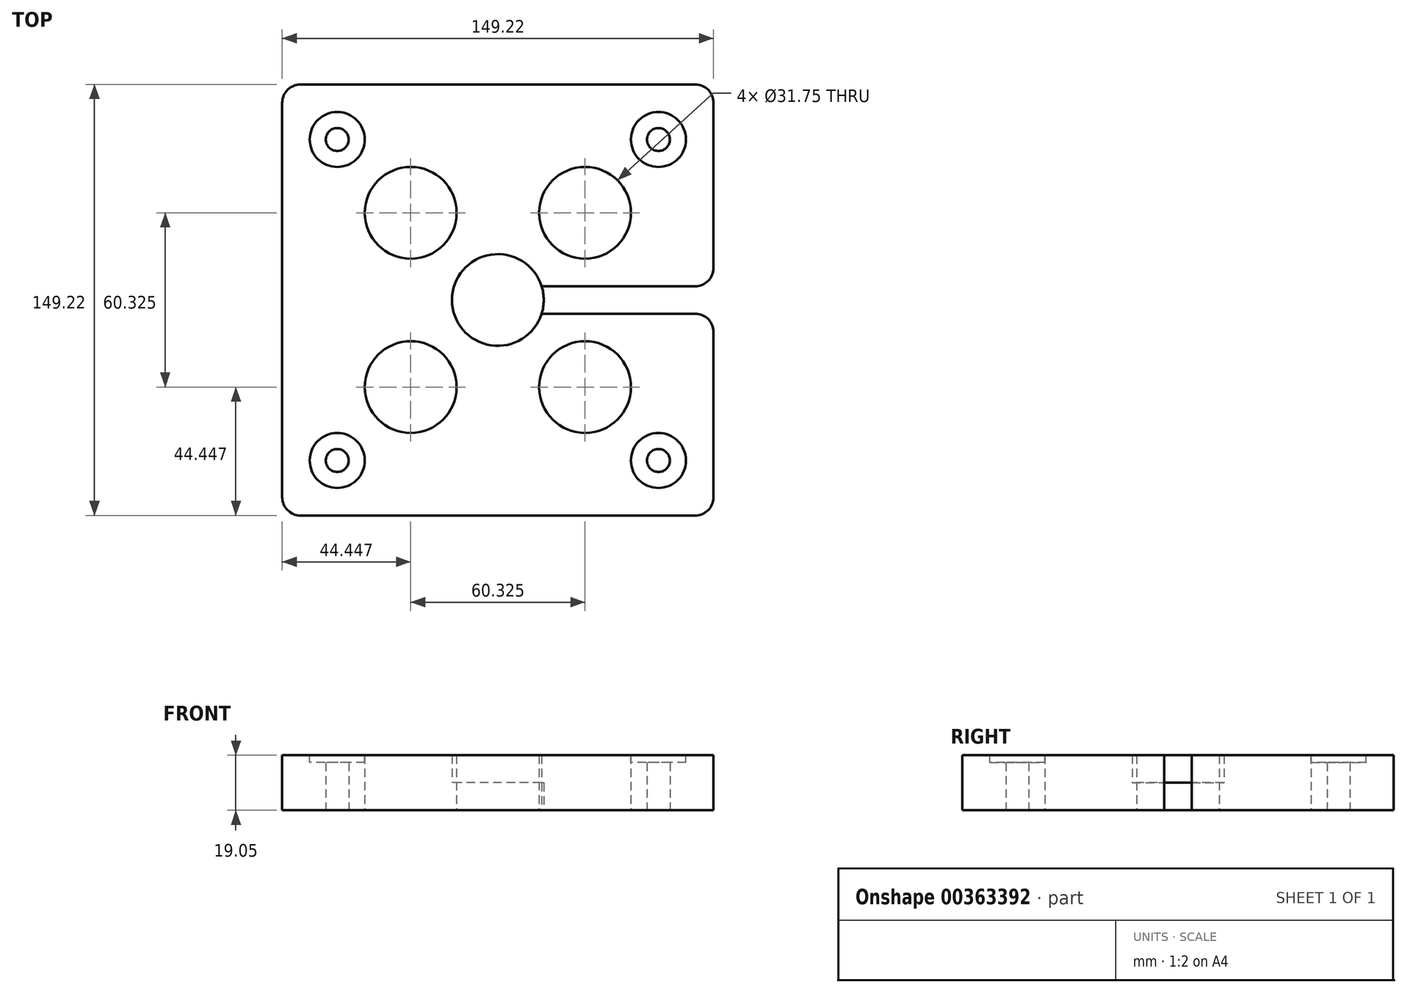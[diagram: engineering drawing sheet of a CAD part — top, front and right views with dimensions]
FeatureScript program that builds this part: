
annotation { "Feature Type Name" : "Feature", "Feature Type Description" : "" }
export const myFeature = defineFeature(function(context is Context, id is Id, definition is map)
    precondition{}
    {
        {
            var Q0;
            Q0=qCreatedBy(makeId("Top.planeOp"),FACE);
            var sketch = newSketch(context, id + "F0", { "sketchPlane" : qUnion([Q0])});
            skLineSegment(sketch, "E0.bottom", {"start": v(68.26, -74.61) * mm, "end": v(-68.26, -74.61) * mm});
            skLineSegment(sketch, "E0.top", {"start": v(68.26, 74.61) * mm, "end": v(-68.26, 74.61) * mm});
            skLineSegment(sketch, "E0.left", {"start": v(74.61, -68.26) * mm, "end": v(74.61, 68.26) * mm});
            skLineSegment(sketch, "E0.right", {"start": v(-74.61, -68.26) * mm, "end": v(-74.61, 68.26) * mm});
            skPoint(sketch, "E0.middle", {"position": v(0, 0) * mm});
            skCircle(sketch, "E1", {"center": v(0, 0) * mm, "radius": 15.88 * mm});
            skCircle(sketch, "E2", {"center": v(-30.16, 30.16) * mm, "radius": 15.88 * mm});
            skCircle(sketch, "E3", {"center": v(30.16, 30.16) * mm, "radius": 15.88 * mm});
            skCircle(sketch, "E4", {"center": v(-30.16, -30.16) * mm, "radius": 15.88 * mm});
            skCircle(sketch, "E5", {"center": v(30.16, -30.16) * mm, "radius": 15.88 * mm});
            skLineSegment(sketch, "E6", {"start": v(15.14, 4.76) * mm, "end": v(74.61, 4.76) * mm});
            skLineSegment(sketch, "E7", {"start": v(15.14, -4.76) * mm, "end": v(74.61, -4.76) * mm});
            skLineSegment(sketch, "E8", {"start": v(74.61, 4.76) * mm, "end": v(74.61, -4.76) * mm});
            skCircle(sketch, "E9", {"center": v(-55.56, 55.56) * mm, "radius": 3.97 * mm});
            skCircle(sketch, "E10", {"center": v(55.56, 55.56) * mm, "radius": 3.98 * mm});
            skCircle(sketch, "E11", {"center": v(-55.56, -55.56) * mm, "radius": 3.98 * mm});
            skCircle(sketch, "E12", {"center": v(55.56, -55.56) * mm, "radius": 3.98 * mm});
            skPoint(sketch, "E13.visualSharp", {"position": v(-74.61, 74.61) * mm});
            skArc(sketch, "E13.filletArc", {"start": v(-68.26, 74.61) * mm, "mid": v(-72.75, 72.75) * mm, "end": v(-74.61, 68.26) * mm});
            skPoint(sketch, "E14.visualSharp", {"position": v(74.61, 74.61) * mm});
            skArc(sketch, "E14.filletArc", {"start": v(74.61, 68.26) * mm, "mid": v(72.75, 72.75) * mm, "end": v(68.26, 74.61) * mm});
            skPoint(sketch, "E15.visualSharp", {"position": v(74.61, -74.61) * mm});
            skArc(sketch, "E15.filletArc", {"start": v(68.26, -74.61) * mm, "mid": v(72.75, -72.75) * mm, "end": v(74.61, -68.26) * mm});
            skPoint(sketch, "E16.visualSharp", {"position": v(-74.61, -74.61) * mm});
            skArc(sketch, "E16.filletArc", {"start": v(-74.61, -68.26) * mm, "mid": v(-72.75, -72.75) * mm, "end": v(-68.26, -74.61) * mm});
            skSolve(sketch);
        }
        {
            var Q0;
            {var subQ3=sQuery(id+"F0.wireOp",EDGE,"E0.bottom");Q0=makeQuery(id+"F0.imprint","IMPRINT",FACE,{"disambiguationData":[TD([[makeQuery(id+"F0.imprint","IMPRINT",EDGE,{"derivedFrom":subQ3}),-1.0]])]});}
            extrude(context, id + "F1", {"entities" : qUnion([Q0]), "depth" : 19.05 * mm});
        }
        {
            var Q0;
            Q0=makeQuery(id+"F1.opExtrude","CAP_FACE",FACE,{"disambiguationData":[OSD([sQuery(id+"F0.wireOp",EDGE,"E0.bottom"),sQuery(id+"F0.wireOp",EDGE,"E0.top"),sQuery(id+"F0.wireOp",EDGE,"E0.left"),sQuery(id+"F0.wireOp",EDGE,"E0.right"),sQuery(id+"F0.wireOp",EDGE,"E1"),sQuery(id+"F0.wireOp",EDGE,"E2"),sQuery(id+"F0.wireOp",EDGE,"E3"),sQuery(id+"F0.wireOp",EDGE,"E4"),sQuery(id+"F0.wireOp",EDGE,"E5"),sQuery(id+"F0.wireOp",EDGE,"E6"),sQuery(id+"F0.wireOp",EDGE,"E7"),sQuery(id+"F0.wireOp",EDGE,"E9"),sQuery(id+"F0.wireOp",EDGE,"E10"),sQuery(id+"F0.wireOp",EDGE,"E11"),sQuery(id+"F0.wireOp",EDGE,"E12")])],"isStart":true});
            var sketch = newSketch(context, id + "F2", { "sketchPlane" : qUnion([Q0])});
            skArc(sketch, "E17", {"start": v(15.14, 4.76) * mm, "mid": v(15.87, 0) * mm, "end": v(15.14, -4.76) * mm});
            skLineSegment(sketch, "E18", {"start": v(74.61, 4.76) * mm, "end": v(74.61, -4.76) * mm});
            skSolve(sketch);
        }
        {
            var Q0;
            Q0=makeQuery(id+"F2.imprint","IMPRINT",FACE,{"disambiguationData":[TD([[makeQuery(id+"F2.imprint","IMPRINT",EDGE,{"derivedFrom":sQuery(id+"F2.wireOp",EDGE,"E17")}),1.0]])]});
            extrude(context, id + "F3", {"entities" : qUnion([Q0]), "operationType" : NewBodyOperationType.ADD, "oppositeDirection" : true, "depth" : 9.52 * mm});
        }
        {
            var Q0;
            Q0=makeQuery(id+"F1.opExtrude","SWEPT_EDGE",EDGE,{"disambiguationData":[OSD([sQuery(id+"F0.wireOp",EDGE,"E0.top"),sQuery(id+"F0.wireOp",EDGE,"E0.right")])]});
            var Q1;
            Q1=makeQuery(id+"F1.opExtrude","SWEPT_EDGE",EDGE,{"disambiguationData":[OSD([sQuery(id+"F0.wireOp",EDGE,"E0.bottom"),sQuery(id+"F0.wireOp",EDGE,"E0.right")])]});
            var Q2;
            Q2=makeQuery(id+"F1.opExtrude","SWEPT_EDGE",EDGE,{"disambiguationData":[OSD([sQuery(id+"F0.wireOp",EDGE,"E0.top"),sQuery(id+"F0.wireOp",EDGE,"E0.left")])]});
            var Q3;
            Q3=makeQuery(id+"F1.opExtrude","SWEPT_EDGE",EDGE,{"disambiguationData":[OSD([sQuery(id+"F0.wireOp",EDGE,"E0.bottom"),sQuery(id+"F0.wireOp",EDGE,"E0.left")])]});
            fillet(context, id + "F4", {"entities" : qUnion([Q0, Q1, Q2, Q3]), "radius" : 6.35 * mm, "tangentPropagation" : true, "allowEdgeOverflow" : false});
        }
        {
            var Q0;
            Q0=makeQuery(id+"F1.opExtrude","CAP_FACE",FACE,{"disambiguationData":[OSD([sQuery(id+"F0.wireOp",EDGE,"E0.bottom"),sQuery(id+"F0.wireOp",EDGE,"E0.top"),sQuery(id+"F0.wireOp",EDGE,"E0.left"),sQuery(id+"F0.wireOp",EDGE,"E0.right"),sQuery(id+"F0.wireOp",EDGE,"E1"),sQuery(id+"F0.wireOp",EDGE,"E2"),sQuery(id+"F0.wireOp",EDGE,"E3"),sQuery(id+"F0.wireOp",EDGE,"E4"),sQuery(id+"F0.wireOp",EDGE,"E5"),sQuery(id+"F0.wireOp",EDGE,"E6"),sQuery(id+"F0.wireOp",EDGE,"E7"),sQuery(id+"F0.wireOp",EDGE,"E9"),sQuery(id+"F0.wireOp",EDGE,"E10"),sQuery(id+"F0.wireOp",EDGE,"E11"),sQuery(id+"F0.wireOp",EDGE,"E12")])],"isStart":false});
            var sketch = newSketch(context, id + "F5", { "sketchPlane" : qUnion([Q0])});
            skCircle(sketch, "E19", {"center": v(-55.56, 55.56) * mm, "radius": 9.53 * mm});
            skCircle(sketch, "E20", {"center": v(55.56, 55.56) * mm, "radius": 9.53 * mm});
            skCircle(sketch, "E21", {"center": v(-55.56, -55.56) * mm, "radius": 9.53 * mm});
            skCircle(sketch, "E22", {"center": v(55.56, -55.56) * mm, "radius": 9.53 * mm});
            skSolve(sketch);
        }
        {
            var Q0;
            Q0=makeQuery(id+"F5.imprint","IMPRINT",FACE,{"disambiguationData":[TD([[makeQuery(id+"F5.imprint","IMPRINT",EDGE,{"derivedFrom":sQuery(id+"F5.wireOp",EDGE,"E21")}),1.0]])]});
            var Q1;
            Q1=makeQuery(id+"F5.imprint","IMPRINT",FACE,{"disambiguationData":[TD([[makeQuery(id+"F5.imprint","IMPRINT",EDGE,{"derivedFrom":sQuery(id+"F5.wireOp",EDGE,"E22")}),1.0]])]});
            var Q2;
            Q2=makeQuery(id+"F5.imprint","IMPRINT",FACE,{"disambiguationData":[TD([[makeQuery(id+"F5.imprint","IMPRINT",EDGE,{"derivedFrom":sQuery(id+"F5.wireOp",EDGE,"E20")}),1.0]])]});
            var Q3;
            Q3=makeQuery(id+"F5.imprint","IMPRINT",FACE,{"disambiguationData":[TD([[makeQuery(id+"F5.imprint","IMPRINT",EDGE,{"derivedFrom":sQuery(id+"F5.wireOp",EDGE,"E19")}),1.0]])]});
            extrude(context, id + "F6", {"entities" : qUnion([Q0, Q1, Q2, Q3]), "operationType" : NewBodyOperationType.REMOVE, "depth" : -2.54 * mm});
        }
    });
